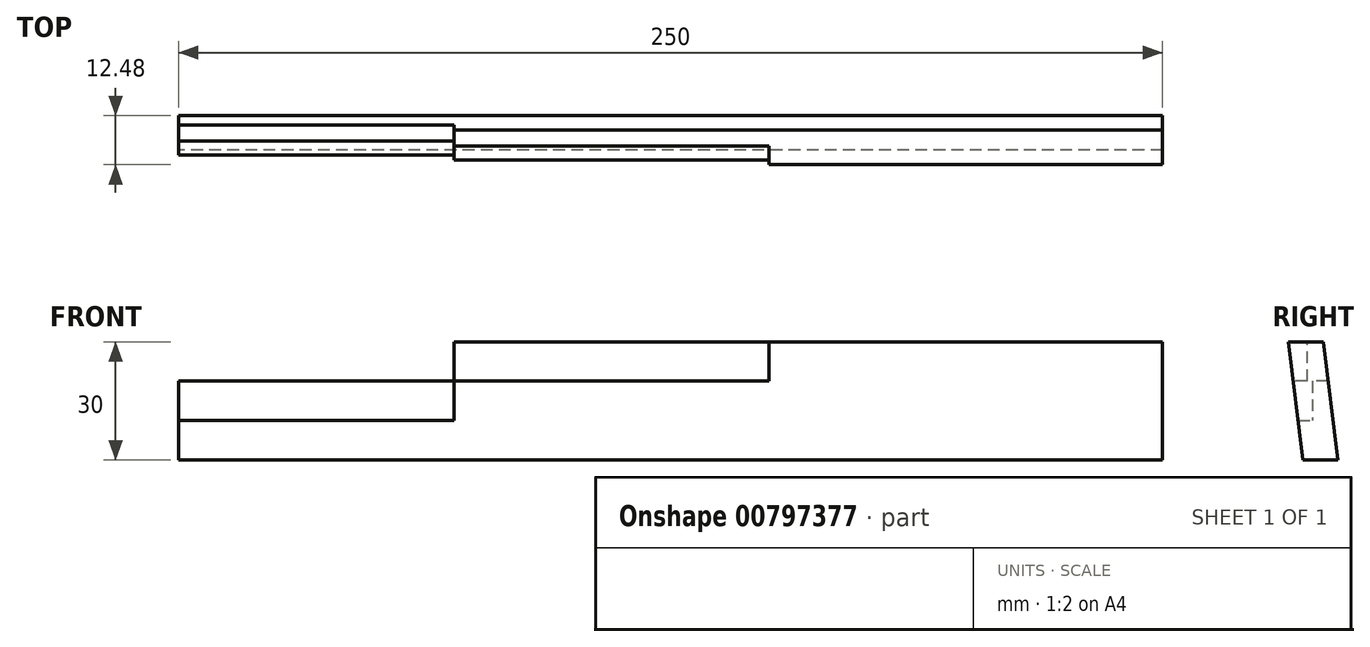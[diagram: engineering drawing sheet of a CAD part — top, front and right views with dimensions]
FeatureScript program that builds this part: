
annotation { "Feature Type Name" : "Feature", "Feature Type Description" : "" }
export const myFeature = defineFeature(function(context is Context, id is Id, definition is map)
    precondition{}
    {
        {
            var Q0;
            Q0=qCreatedBy(makeId("Right.planeOp"),FACE);
            var sketch = newSketch(context, id + "F0", { "sketchPlane" : qUnion([Q0])});
            skLineSegment(sketch, "E0", {"start": v(0, 0) * mm, "end": v(-1.23, 10) * mm});
            skLineSegment(sketch, "E1", {"start": v(0, 0) * mm, "end": v(-8.8, 0) * mm});
            skLineSegment(sketch, "E2", {"start": v(-8.8, 0) * mm, "end": v(-10.03, 10) * mm});
            skLineSegment(sketch, "E3", {"start": v(-10.03, 10) * mm, "end": v(-1.23, 10) * mm});
            skSolve(sketch);
        }
        {
            var Q0;
            Q0=makeQuery(id+"F0.imprint","IMPRINT",FACE,{"disambiguationData":[TD([[makeQuery(id+"F0.imprint","IMPRINT",EDGE,{"derivedFrom":sQuery(id+"F0.wireOp",EDGE,"E0")}),1.0]])]});
            extrude(context, id + "F1", {"entities" : qUnion([Q0]), "depth" : 70 * mm, "offsetDistance" : 25 * mm});
        }
        {
            var Q0;
            Q0=makeQuery(id+"F1.opExtrude","CAP_FACE",FACE,{"disambiguationData":[OSD([sQuery(id+"F0.wireOp",EDGE,"E0"),sQuery(id+"F0.wireOp",EDGE,"E1"),sQuery(id+"F0.wireOp",EDGE,"E2"),sQuery(id+"F0.wireOp",EDGE,"E3")])],"isStart":false});
            var sketch = newSketch(context, id + "F2", { "sketchPlane" : qUnion([Q0])});
            skLineSegment(sketch, "E4", {"start": v(-1.23, 10) * mm, "end": v(-2.46, 20) * mm});
            skLineSegment(sketch, "E5", {"start": v(-2.46, 20) * mm, "end": v(-11.26, 20) * mm});
            skLineSegment(sketch, "E6", {"start": v(-11.26, 20) * mm, "end": v(-10.03, 10) * mm});
            skLineSegment(sketch, "E7.0.0", {"start": v(-1.23, 10) * mm, "end": v(-10.03, 10) * mm});
            skLineSegment(sketch, "E7.0.1", {"start": v(-10.03, 10) * mm, "end": v(-8.8, 0) * mm});
            skLineSegment(sketch, "E7.0.2", {"start": v(-8.8, 0) * mm, "end": v(0, 0) * mm});
            skLineSegment(sketch, "E7.0.3", {"start": v(0, 0) * mm, "end": v(-1.23, 10) * mm});
            skSolve(sketch);
        }
        {
            var Q0;
            Q0=makeQuery(id+"F2.imprint","IMPRINT",FACE,{"disambiguationData":[TD([[makeQuery(id+"F2.imprint","IMPRINT",EDGE,{"derivedFrom":sQuery(id+"F2.wireOp",EDGE,"E7.0.0")}),-1.0]])]});
            var Q1;
            Q1=makeQuery(id+"F2.imprint","IMPRINT",FACE,{"disambiguationData":[TD([[makeQuery(id+"F2.imprint","IMPRINT",EDGE,{"derivedFrom":sQuery(id+"F2.wireOp",EDGE,"E4")}),1.0]])]});
            extrude(context, id + "F3", {"entities" : qUnion([Q0, Q1]), "operationType" : NewBodyOperationType.ADD, "depth" : 80 * mm, "offsetDistance" : 25 * mm});
        }
        {
            var Q0;
            Q0=makeQuery(id+"F3.opExtrude","CAP_FACE",FACE,{"disambiguationData":[OSD([sQuery(id+"F2.wireOp",EDGE,"E4"),sQuery(id+"F2.wireOp",EDGE,"E5"),sQuery(id+"F2.wireOp",EDGE,"E6"),sQuery(id+"F2.wireOp",EDGE,"E7.0.1"),sQuery(id+"F2.wireOp",EDGE,"E7.0.2"),sQuery(id+"F2.wireOp",EDGE,"E7.0.3")])],"isStart":false});
            var sketch = newSketch(context, id + "F4", { "sketchPlane" : qUnion([Q0])});
            skLineSegment(sketch, "E8.0.0", {"start": v(0, 0) * mm, "end": v(-2.46, 20) * mm});
            skLineSegment(sketch, "E8.0.1", {"start": v(-2.46, 20) * mm, "end": v(-11.26, 20) * mm});
            skLineSegment(sketch, "E8.0.2", {"start": v(-11.26, 20) * mm, "end": v(-8.8, 0) * mm});
            skLineSegment(sketch, "E8.0.3", {"start": v(-8.8, 0) * mm, "end": v(0, 0) * mm});
            skLineSegment(sketch, "E9", {"start": v(-2.46, 20) * mm, "end": v(-3.68, 30) * mm});
            skLineSegment(sketch, "E10", {"start": v(-3.68, 30) * mm, "end": v(-12.48, 30) * mm});
            skLineSegment(sketch, "E11", {"start": v(-12.48, 30) * mm, "end": v(-11.26, 20) * mm});
            skSolve(sketch);
        }
        {
            var Q0;
            Q0 = qSketchRegion(id + "F4", true);
            extrude(context, id + "F5", {"entities" : qUnion([Q0]), "operationType" : NewBodyOperationType.ADD, "depth" : 100 * mm, "offsetDistance" : 25 * mm});
        }
        {
            var Q0;
            Q0=makeQuery(id+"F3.opExtrude","SWEPT_FACE",FACE,{"disambiguationData":[OSD([sQuery(id+"F2.wireOp",EDGE,"E5")])]});
            var sketch = newSketch(context, id + "F6", { "sketchPlane" : qUnion([Q0])});
            skLineSegment(sketch, "E12", {"start": v(150, -2.46) * mm, "end": v(150, -6.46) * mm});
            skLineSegment(sketch, "E13", {"start": v(150, -6.46) * mm, "end": v(70, -6.46) * mm});
            skLineSegment(sketch, "E14", {"start": v(70, -6.46) * mm, "end": v(70, -2.46) * mm});
            skLineSegment(sketch, "E15", {"start": v(70, -6.46) * mm, "end": v(0, -6.46) * mm});
            skLineSegment(sketch, "E16.0", {"start": v(70, -1.23) * mm, "end": v(0, -1.23) * mm});
            skLineSegment(sketch, "E17.0", {"start": v(0, -10.03) * mm, "end": v(0, -1.23) * mm});
            skLineSegment(sketch, "E18.0.0", {"start": v(150, -3.68) * mm, "end": v(150, -12.48) * mm});
            skLineSegment(sketch, "E18.0.1", {"start": v(150, -12.48) * mm, "end": v(250, -12.48) * mm});
            skLineSegment(sketch, "E18.0.2", {"start": v(250, -12.48) * mm, "end": v(250, -3.68) * mm});
            skLineSegment(sketch, "E18.0.3", {"start": v(250, -3.68) * mm, "end": v(150, -3.68) * mm});
            skLineSegment(sketch, "E19", {"start": v(150, -6.46) * mm, "end": v(250, -6.46) * mm});
            skLineSegment(sketch, "E20", {"start": v(70, -2.46) * mm, "end": v(0, -2.46) * mm});
            skSolve(sketch);
        }
        {
            var Q0;
            Q0=makeQuery(id+"F1.opExtrude","CAP_FACE",FACE,{"disambiguationData":[OSD([sQuery(id+"F0.wireOp",EDGE,"E0"),sQuery(id+"F0.wireOp",EDGE,"E1"),sQuery(id+"F0.wireOp",EDGE,"E2"),sQuery(id+"F0.wireOp",EDGE,"E3")])],"isStart":true});
            var sketch = newSketch(context, id + "F7", { "sketchPlane" : qUnion([Q0])});
            skPoint(sketch, "E21.0", {"position": v(2.46, 20) * mm});
            skPoint(sketch, "E22.0", {"position": v(6.46, 20) * mm});
            skLineSegment(sketch, "E23", {"start": v(1.23, 10) * mm, "end": v(2.46, 20) * mm});
            skLineSegment(sketch, "E24", {"start": v(2.46, 20) * mm, "end": v(6.46, 20) * mm});
            skLineSegment(sketch, "E25", {"start": v(6.46, 20) * mm, "end": v(6.46, 10) * mm});
            skLineSegment(sketch, "E26", {"start": v(6.46, 10) * mm, "end": v(1.23, 10) * mm});
            skSolve(sketch);
        }
        {
            var Q0;
            Q0 = qSketchRegion(id + "F7", true);
            extrude(context, id + "F8", {"entities" : qUnion([Q0]), "operationType" : NewBodyOperationType.ADD, "oppositeDirection" : true, "depth" : 70 * mm, "offsetDistance" : 25 * mm});
        }
        {
            var Q0;
            Q0=makeQuery(id+"F5.opExtrude","CAP_FACE",FACE,{"disambiguationData":[OSD([sQuery(id+"F4.wireOp",EDGE,"E8.0.0"),sQuery(id+"F4.wireOp",EDGE,"E8.0.2"),sQuery(id+"F4.wireOp",EDGE,"E8.0.3"),sQuery(id+"F4.wireOp",EDGE,"E9"),sQuery(id+"F4.wireOp",EDGE,"E10"),sQuery(id+"F4.wireOp",EDGE,"E11")])],"isStart":true});
            var sketch = newSketch(context, id + "F9", { "sketchPlane" : qUnion([Q0])});
            skLineSegment(sketch, "E27", {"start": v(7.68, 20) * mm, "end": v(7.68, 30) * mm});
            skLineSegment(sketch, "E28", {"start": v(7.68, 30) * mm, "end": v(3.68, 30) * mm});
            skLineSegment(sketch, "E29", {"start": v(3.68, 30) * mm, "end": v(2.46, 20) * mm});
            skSolve(sketch);
        }
        {
            var Q0;
            {var subQ0=sQuery(id+"F9.wireOp",EDGE,"E27");Q0=makeQuery(id+"F9.imprint","IMPRINT",FACE,{"disambiguationData":[TD([[makeQuery(id+"F9.imprint","IMPRINT",EDGE,{"derivedFrom":subQ0}),1.0]])]});}
            extrude(context, id + "F10", {"entities" : qUnion([Q0]), "operationType" : NewBodyOperationType.ADD, "depth" : 80 * mm, "offsetDistance" : 25 * mm});
        }
    });
